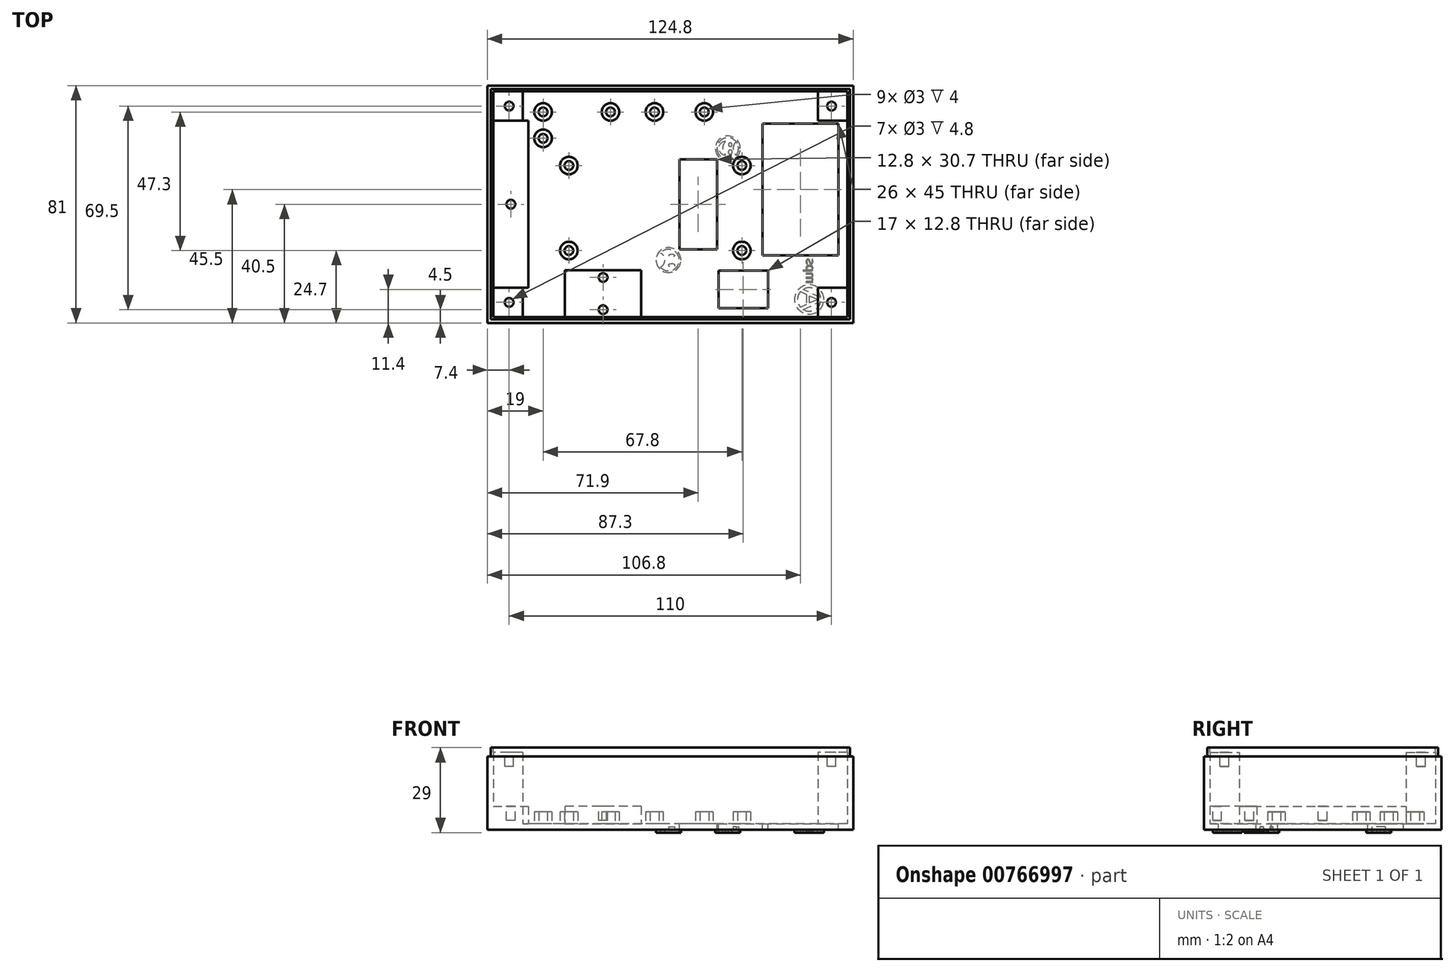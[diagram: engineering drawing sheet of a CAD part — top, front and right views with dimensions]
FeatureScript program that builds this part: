
annotation { "Feature Type Name" : "Feature", "Feature Type Description" : "" }
export const myFeature = defineFeature(function(context is Context, id is Id, definition is map)
    precondition{}
    {
        {
            var Q0;
            Q0=qCreatedBy(makeId("Top.planeOp"),FACE);
            var sketch = newSketch(context, id + "F0", { "sketchPlane" : qUnion([Q0])});
            skLineSegment(sketch, "E0.bottom", {"start": v(62.4, -40.5) * mm, "end": v(-62.4, -40.5) * mm});
            skLineSegment(sketch, "E0.top", {"start": v(62.4, 40.5) * mm, "end": v(-62.4, 40.5) * mm});
            skLineSegment(sketch, "E0.left", {"start": v(62.4, -40.5) * mm, "end": v(62.4, 40.5) * mm});
            skLineSegment(sketch, "E0.right", {"start": v(-62.4, -40.5) * mm, "end": v(-62.4, 40.5) * mm});
            skPoint(sketch, "E0.middle", {"position": v(0, 0) * mm});
            skSolve(sketch);
        }
        {
            var Q0;
            Q0=qSketchRegion(id+"F0",true);
            extrude(context, id + "F1", {"entities" : qUnion([Q0]), "depth" : 25 * mm, "offsetDistance" : 25 * mm});
        }
        {
            var Q0;
            Q0=makeQuery(id+"F1.opExtrude","CAP_FACE",FACE,{"disambiguationData":[OSD([sQuery(id+"F0.wireOp",EDGE,"E0.bottom"),sQuery(id+"F0.wireOp",EDGE,"E0.top"),sQuery(id+"F0.wireOp",EDGE,"E0.left"),sQuery(id+"F0.wireOp",EDGE,"E0.right")])],"isStart":false});
            var sketch = newSketch(context, id + "F2", { "sketchPlane" : qUnion([Q0])});
            skLineSegment(sketch, "E1.bottom", {"start": v(61.25, -39.35) * mm, "end": v(-61.25, -39.35) * mm});
            skLineSegment(sketch, "E1.top", {"start": v(61.25, 39.35) * mm, "end": v(-61.25, 39.35) * mm});
            skLineSegment(sketch, "E1.left", {"start": v(61.25, -39.35) * mm, "end": v(61.25, 39.35) * mm});
            skLineSegment(sketch, "E1.right", {"start": v(-61.25, -39.35) * mm, "end": v(-61.25, 39.35) * mm});
            skPoint(sketch, "E1.middle", {"position": v(0, 0) * mm});
            skSolve(sketch);
        }
        {
            var Q0;
            Q0=qSketchRegion(id+"F2",true);
            extrude(context, id + "F3", {"entities" : qUnion([Q0]), "operationType" : NewBodyOperationType.ADD, "depth" : 3 * mm, "offsetDistance" : 25 * mm});
        }
        {
            var Q0;
            Q0=makeQuery(id+"F3.opExtrude","CAP_FACE",FACE,{"disambiguationData":[OSD([sQuery(id+"F2.wireOp",EDGE,"E1.bottom"),sQuery(id+"F2.wireOp",EDGE,"E1.top"),sQuery(id+"F2.wireOp",EDGE,"E1.left"),sQuery(id+"F2.wireOp",EDGE,"E1.right")])],"isStart":false});
            var sketch = newSketch(context, id + "F4", { "sketchPlane" : qUnion([Q0])});
            skLineSegment(sketch, "E2.bottom", {"start": v(60.4, -38.5) * mm, "end": v(-60.4, -38.5) * mm});
            skLineSegment(sketch, "E2.top", {"start": v(60.4, 38.5) * mm, "end": v(-60.4, 38.5) * mm});
            skLineSegment(sketch, "E2.left", {"start": v(60.4, -38.5) * mm, "end": v(60.4, 38.5) * mm});
            skLineSegment(sketch, "E2.right", {"start": v(-60.4, -38.5) * mm, "end": v(-60.4, 38.5) * mm});
            skPoint(sketch, "E2.middle", {"position": v(0, 0) * mm});
            skSolve(sketch);
        }
        {
            var Q0;
            Q0=qSketchRegion(id+"F4",true);
            extrude(context, id + "F5", {"entities" : qUnion([Q0]), "operationType" : NewBodyOperationType.REMOVE, "oppositeDirection" : true, "depth" : 26 * mm, "offsetDistance" : 25 * mm});
        }
        {
            var Q0;
            Q0=makeQuery(id+"F5.boolean.opBoolean","COPY",FACE,{"derivedFrom":makeQuery(id+"F5.opExtrude","CAP_FACE",FACE,{"disambiguationData":[OSD([sQuery(id+"F4.wireOp",EDGE,"E2.bottom"),sQuery(id+"F4.wireOp",EDGE,"E2.top"),sQuery(id+"F4.wireOp",EDGE,"E2.left"),sQuery(id+"F4.wireOp",EDGE,"E2.right")])],"isStart":false})});
            var sketch = newSketch(context, id + "F6", { "sketchPlane" : qUnion([Q0])});
            skLineSegment(sketch, "E3.bottom", {"start": v(-60.4, 38.5) * mm, "end": v(-50.4, 38.5) * mm});
            skLineSegment(sketch, "E3.top", {"start": v(-60.4, 28.5) * mm, "end": v(-50.4, 28.5) * mm});
            skLineSegment(sketch, "E3.left", {"start": v(-60.4, 38.5) * mm, "end": v(-60.4, 28.5) * mm});
            skLineSegment(sketch, "E3.right", {"start": v(-50.4, 38.5) * mm, "end": v(-50.4, 28.5) * mm});
            skLineSegment(sketch, "E4.bottom", {"start": v(-60.4, -38.5) * mm, "end": v(-50.4, -38.5) * mm});
            skLineSegment(sketch, "E4.top", {"start": v(-60.4, -28.5) * mm, "end": v(-50.4, -28.5) * mm});
            skLineSegment(sketch, "E4.left", {"start": v(-60.4, -38.5) * mm, "end": v(-60.4, -28.5) * mm});
            skLineSegment(sketch, "E4.right", {"start": v(-50.4, -38.5) * mm, "end": v(-50.4, -28.5) * mm});
            skLineSegment(sketch, "E5.bottom", {"start": v(60.4, -38.5) * mm, "end": v(50.4, -38.5) * mm});
            skLineSegment(sketch, "E5.top", {"start": v(60.4, -28.5) * mm, "end": v(50.4, -28.5) * mm});
            skLineSegment(sketch, "E5.left", {"start": v(60.4, -38.5) * mm, "end": v(60.4, -28.5) * mm});
            skLineSegment(sketch, "E5.right", {"start": v(50.4, -38.5) * mm, "end": v(50.4, -28.5) * mm});
            skLineSegment(sketch, "E6.bottom", {"start": v(60.4, 38.5) * mm, "end": v(50.4, 38.5) * mm});
            skLineSegment(sketch, "E6.top", {"start": v(60.4, 28.5) * mm, "end": v(50.4, 28.5) * mm});
            skLineSegment(sketch, "E6.left", {"start": v(60.4, 38.5) * mm, "end": v(60.4, 28.5) * mm});
            skLineSegment(sketch, "E6.right", {"start": v(50.4, 38.5) * mm, "end": v(50.4, 28.5) * mm});
            skSolve(sketch);
        }
        {
            var Q0;
            Q0=qSketchRegion(id+"F6",true);
            extrude(context, id + "F7", {"entities" : qUnion([Q0]), "operationType" : NewBodyOperationType.ADD, "depth" : 24.4 * mm, "offsetDistance" : 25 * mm});
        }
        {
            var Q0;
            Q0=makeQuery(id+"F7.opExtrude","CAP_FACE",FACE,{"disambiguationData":[OSD([sQuery(id+"F6.wireOp",EDGE,"E3.bottom"),sQuery(id+"F6.wireOp",EDGE,"E3.top"),sQuery(id+"F6.wireOp",EDGE,"E3.left"),sQuery(id+"F6.wireOp",EDGE,"E3.right")])],"isStart":false});
            var sketch = newSketch(context, id + "F8", { "sketchPlane" : qUnion([Q0])});
            skCircle(sketch, "E7", {"center": v(-55, 33.5) * mm, "radius": 1.5 * mm});
            skPoint(sketch, "E7.centerSnap0", {"position": v(-50.4, 33.5) * mm});
            skCircle(sketch, "E8", {"center": v(-55, -33.5) * mm, "radius": 1.5 * mm});
            skCircle(sketch, "E9", {"center": v(55, -33.5) * mm, "radius": 1.5 * mm});
            skCircle(sketch, "E10", {"center": v(55, 33.5) * mm, "radius": 1.5 * mm});
            skSolve(sketch);
        }
        {
            var Q0;
            Q0=qSketchRegion(id+"F8",true);
            extrude(context, id + "F9", {"entities" : qUnion([Q0]), "operationType" : NewBodyOperationType.REMOVE, "oppositeDirection" : true, "depth" : 4.8 * mm, "offsetDistance" : 25 * mm});
        }
        {
            var Q0;
            Q0=makeQuery(id+"F5.boolean.opBoolean","COPY",FACE,{"derivedFrom":makeQuery(id+"F5.opExtrude","CAP_FACE",FACE,{"disambiguationData":[OSD([sQuery(id+"F4.wireOp",EDGE,"E2.bottom"),sQuery(id+"F4.wireOp",EDGE,"E2.top"),sQuery(id+"F4.wireOp",EDGE,"E2.left"),sQuery(id+"F4.wireOp",EDGE,"E2.right")])],"isStart":false})});
            var sketch = newSketch(context, id + "F10", { "sketchPlane" : qUnion([Q0])});
            skLineSegment(sketch, "E11.bottom", {"start": v(31.4, 27.5) * mm, "end": v(57.4, 27.5) * mm});
            skLineSegment(sketch, "E11.top", {"start": v(31.4, -17.5) * mm, "end": v(57.4, -17.5) * mm});
            skLineSegment(sketch, "E11.left", {"start": v(31.4, 27.5) * mm, "end": v(31.4, -17.5) * mm});
            skLineSegment(sketch, "E11.right", {"start": v(57.4, 27.5) * mm, "end": v(57.4, -17.5) * mm});
            skLineSegment(sketch, "E12.bottom", {"start": v(16.4, -22.7) * mm, "end": v(33.4, -22.7) * mm});
            skLineSegment(sketch, "E12.top", {"start": v(16.4, -35.5) * mm, "end": v(33.4, -35.5) * mm});
            skLineSegment(sketch, "E12.left", {"start": v(16.4, -22.7) * mm, "end": v(16.4, -35.5) * mm});
            skLineSegment(sketch, "E12.right", {"start": v(33.4, -22.7) * mm, "end": v(33.4, -35.5) * mm});
            skLineSegment(sketch, "E13.bottom", {"start": v(15.9, -15.35) * mm, "end": v(3.1, -15.35) * mm});
            skLineSegment(sketch, "E13.top", {"start": v(15.9, 15.35) * mm, "end": v(3.1, 15.35) * mm});
            skLineSegment(sketch, "E13.left", {"start": v(15.9, -15.35) * mm, "end": v(15.9, 15.35) * mm});
            skLineSegment(sketch, "E13.right", {"start": v(3.1, -15.35) * mm, "end": v(3.1, 15.35) * mm});
            skPoint(sketch, "E13.middle", {"position": v(9.5, 0) * mm});
            skSolve(sketch);
        }
        {
            var Q0;
            Q0=qSketchRegion(id+"F10",true);
            extrude(context, id + "F11", {"entities" : qUnion([Q0]), "operationType" : NewBodyOperationType.REMOVE, "endBound" : BoundingType.THROUGH_ALL, "oppositeDirection" : true, "depth" : 25 * mm, "offsetDistance" : 25 * mm});
        }
        {
            var Q0;
            Q0=makeQuery(id+"F5.boolean.opBoolean","COPY",FACE,{"derivedFrom":makeQuery(id+"F5.opExtrude","CAP_FACE",FACE,{"disambiguationData":[OSD([sQuery(id+"F4.wireOp",EDGE,"E2.bottom"),sQuery(id+"F4.wireOp",EDGE,"E2.top"),sQuery(id+"F4.wireOp",EDGE,"E2.left"),sQuery(id+"F4.wireOp",EDGE,"E2.right")])],"isStart":false})});
            var sketch = newSketch(context, id + "F12", { "sketchPlane" : qUnion([Q0])});
            skCircle(sketch, "E14", {"center": v(24.4, 13.2) * mm, "radius": 3 * mm});
            skCircle(sketch, "E15", {"center": v(-34.6, 13.2) * mm, "radius": 3 * mm});
            skCircle(sketch, "E16", {"center": v(-34.6, -15.8) * mm, "radius": 3 * mm});
            skCircle(sketch, "E17", {"center": v(24.4, -15.8) * mm, "radius": 3 * mm});
            skCircle(sketch, "E18", {"center": v(-43.4, 31.5) * mm, "radius": 3 * mm});
            skCircle(sketch, "E19", {"center": v(-43.4, 22.5) * mm, "radius": 3 * mm});
            skCircle(sketch, "E20", {"center": v(-20.4, 31.5) * mm, "radius": 3 * mm});
            skCircle(sketch, "E21", {"center": v(-5.4, 31.5) * mm, "radius": 3 * mm});
            skCircle(sketch, "E22", {"center": v(11.6, 31.5) * mm, "radius": 3 * mm});
            skSolve(sketch);
        }
        {
            var Q0;
            Q0=qSketchRegion(id+"F12",true);
            extrude(context, id + "F13", {"entities" : qUnion([Q0]), "operationType" : NewBodyOperationType.ADD, "depth" : 4 * mm, "offsetDistance" : 25 * mm});
        }
        {
            var Q0;
            Q0=makeQuery(id+"F5.boolean.opBoolean","COPY",FACE,{"derivedFrom":makeQuery(id+"F5.opExtrude","CAP_FACE",FACE,{"disambiguationData":[OSD([sQuery(id+"F4.wireOp",EDGE,"E2.bottom"),sQuery(id+"F4.wireOp",EDGE,"E2.top"),sQuery(id+"F4.wireOp",EDGE,"E2.left"),sQuery(id+"F4.wireOp",EDGE,"E2.right")])],"isStart":false})});
            var sketch = newSketch(context, id + "F14", { "sketchPlane" : qUnion([Q0])});
            skCircle(sketch, "E23", {"center": v(-34.6, -15.8) * mm, "radius": 1.5 * mm});
            skCircle(sketch, "E24", {"center": v(24.4, -15.8) * mm, "radius": 1.5 * mm});
            skCircle(sketch, "E25", {"center": v(-34.6, 13.2) * mm, "radius": 1.5 * mm});
            skCircle(sketch, "E26", {"center": v(24.4, 13.2) * mm, "radius": 1.5 * mm});
            skCircle(sketch, "E27", {"center": v(11.6, 31.5) * mm, "radius": 1.5 * mm});
            skCircle(sketch, "E28", {"center": v(-5.4, 31.5) * mm, "radius": 1.5 * mm});
            skCircle(sketch, "E29", {"center": v(-20.4, 31.5) * mm, "radius": 1.5 * mm});
            skCircle(sketch, "E30", {"center": v(-43.4, 22.5) * mm, "radius": 1.5 * mm});
            skCircle(sketch, "E31", {"center": v(-43.4, 31.5) * mm, "radius": 1.5 * mm});
            skSolve(sketch);
        }
        {
            var Q0;
            Q0=qSketchRegion(id+"F14",true);
            extrude(context, id + "F15", {"entities" : qUnion([Q0]), "operationType" : NewBodyOperationType.REMOVE, "depth" : 4.8 * mm, "offsetDistance" : 25 * mm});
        }
        {
            var Q0;
            Q0=makeQuery(id+"F5.boolean.opBoolean","COPY",FACE,{"derivedFrom":makeQuery(id+"F5.opExtrude","CAP_FACE",FACE,{"disambiguationData":[OSD([sQuery(id+"F4.wireOp",EDGE,"E2.bottom"),sQuery(id+"F4.wireOp",EDGE,"E2.top"),sQuery(id+"F4.wireOp",EDGE,"E2.left"),sQuery(id+"F4.wireOp",EDGE,"E2.right")])],"isStart":false})});
            var sketch = newSketch(context, id + "F16", { "sketchPlane" : qUnion([Q0])});
            skLineSegment(sketch, "E32.bottom", {"start": v(-60.4, -28.5) * mm, "end": v(-48.4, -28.5) * mm});
            skLineSegment(sketch, "E32.top", {"start": v(-60.4, 28.5) * mm, "end": v(-48.4, 28.5) * mm});
            skLineSegment(sketch, "E32.left", {"start": v(-60.4, -28.5) * mm, "end": v(-60.4, 28.5) * mm});
            skLineSegment(sketch, "E32.right", {"start": v(-48.4, -28.5) * mm, "end": v(-48.4, 28.5) * mm});
            skSolve(sketch);
        }
        {
            var Q0;
            Q0=qSketchRegion(id+"F16",true);
            extrude(context, id + "F17", {"entities" : qUnion([Q0]), "operationType" : NewBodyOperationType.ADD, "depth" : 6 * mm, "offsetDistance" : 25 * mm});
        }
        {
            var Q0;
            Q0=makeQuery(id+"F17.opExtrude","CAP_FACE",FACE,{"disambiguationData":[OSD([sQuery(id+"F16.wireOp",EDGE,"E32.bottom"),sQuery(id+"F16.wireOp",EDGE,"E32.top"),sQuery(id+"F16.wireOp",EDGE,"E32.left"),sQuery(id+"F16.wireOp",EDGE,"E32.right")])],"isStart":false});
            var sketch = newSketch(context, id + "F18", { "sketchPlane" : qUnion([Q0])});
            skCircle(sketch, "E33", {"center": v(-54.4, 0) * mm, "radius": 1.5 * mm});
            skPoint(sketch, "E33.centerSnap0", {"position": v(-48.4, 0) * mm});
            skSolve(sketch);
        }
        {
            var Q0;
            Q0=qSketchRegion(id+"F18",true);
            extrude(context, id + "F19", {"entities" : qUnion([Q0]), "operationType" : NewBodyOperationType.REMOVE, "oppositeDirection" : true, "depth" : 4.8 * mm, "offsetDistance" : 25 * mm});
        }
        {
            var Q0;
            Q0=makeQuery(id+"F5.boolean.opBoolean","COPY",FACE,{"derivedFrom":makeQuery(id+"F5.opExtrude","CAP_FACE",FACE,{"disambiguationData":[OSD([sQuery(id+"F4.wireOp",EDGE,"E2.bottom"),sQuery(id+"F4.wireOp",EDGE,"E2.top"),sQuery(id+"F4.wireOp",EDGE,"E2.left"),sQuery(id+"F4.wireOp",EDGE,"E2.right")])],"isStart":false})});
            var sketch = newSketch(context, id + "F20", { "sketchPlane" : qUnion([Q0])});
            skLineSegment(sketch, "E34.bottom", {"start": v(-35.93, -22.5) * mm, "end": v(-9.93, -22.5) * mm});
            skLineSegment(sketch, "E34.top", {"start": v(-35.93, -38.5) * mm, "end": v(-9.93, -38.5) * mm});
            skLineSegment(sketch, "E34.left", {"start": v(-35.93, -22.5) * mm, "end": v(-35.93, -38.5) * mm});
            skLineSegment(sketch, "E34.right", {"start": v(-9.93, -22.5) * mm, "end": v(-9.93, -38.5) * mm});
            skSolve(sketch);
        }
        {
            var Q0;
            Q0=qSketchRegion(id+"F20",true);
            extrude(context, id + "F21", {"entities" : qUnion([Q0]), "operationType" : NewBodyOperationType.ADD, "depth" : 6 * mm, "offsetDistance" : 25 * mm});
        }
        {
            var Q0;
            Q0=makeQuery(id+"F21.opExtrude","CAP_FACE",FACE,{"disambiguationData":[OSD([sQuery(id+"F20.wireOp",EDGE,"E34.bottom"),sQuery(id+"F20.wireOp",EDGE,"E34.top"),sQuery(id+"F20.wireOp",EDGE,"E34.left"),sQuery(id+"F20.wireOp",EDGE,"E34.right")])],"isStart":false});
            var sketch = newSketch(context, id + "F22", { "sketchPlane" : qUnion([Q0])});
            skCircle(sketch, "E35", {"center": v(-22.93, -25) * mm, "radius": 1.5 * mm});
            skPoint(sketch, "E35.centerSnap0", {"position": v(-22.93, -22.5) * mm});
            skPoint(sketch, "E35.perimeterSnap0", {"position": v(-22.93, -22.5) * mm});
            skPoint(sketch, "E35.perimeterSnap1", {"position": v(-35.93, -30.5) * mm});
            skCircle(sketch, "E36", {"center": v(-22.93, -36) * mm, "radius": 1.5 * mm});
            skSolve(sketch);
        }
        {
            var Q0;
            Q0=qSketchRegion(id+"F22",true);
            extrude(context, id + "F23", {"entities" : qUnion([Q0]), "operationType" : NewBodyOperationType.REMOVE, "oppositeDirection" : true, "depth" : 4.8 * mm, "offsetDistance" : 25 * mm});
        }
        {
            var Q0;
            Q0=makeQuery(id+"F1.opExtrude","CAP_FACE",FACE,{"disambiguationData":[OSD([sQuery(id+"F0.wireOp",EDGE,"E0.bottom"),sQuery(id+"F0.wireOp",EDGE,"E0.top"),sQuery(id+"F0.wireOp",EDGE,"E0.left"),sQuery(id+"F0.wireOp",EDGE,"E0.right")])],"isStart":true});
            var sketch = newSketch(context, id + "F24", { "sketchPlane" : qUnion([Q0])});
            skCircle(sketch, "E37", {"center": v(47.4, 32.5) * mm, "radius": 5 * mm});
            skCircle(sketch, "E38", {"center": v(47.4, 32.5) * mm, "radius": 4 * mm});
            skSolve(sketch);
        }
        {
            var Q0;
            Q0 = qSketchRegion(id + "F24", true);
            extrude(context, id + "F25", {"entities" : qUnion([Q0]), "operationType" : NewBodyOperationType.ADD, "depth" : 1 * mm, "offsetDistance" : 25 * mm});
        }
        {
            var Q0;
            {var subQ0=sQuery(id+"F0.wireOp",EDGE,"E0.bottom");var subQ1=sQuery(id+"F0.wireOp",EDGE,"E0.right");var subQ2=sQuery(id+"F0.wireOp",EDGE,"E0.top");var subQ3=sQuery(id+"F0.wireOp",EDGE,"E0.left");Q0=makeQuery(id+"F25.boolean.opBoolean","SPLIT",FACE,{"disambiguationData":[TD([makeQuery(id+"F1.opExtrude","SWEPT_FACE",FACE,{"disambiguationData":[OSD([subQ0])]})])],"derivedFrom":makeQuery(id+"F1.opExtrude","CAP_FACE",FACE,{"disambiguationData":[OSD([subQ0,subQ2,subQ3,subQ1])],"isStart":true})});}
            var sketch = newSketch(context, id + "F26", { "sketchPlane" : qUnion([Q0])});
            skText(sketch, "E39", { "text": "mps", "fontName": "OpenSans-Regular.ttf"});
            const initialGuessF26  = {"E39": [0.04636, 0.0271, 0, -1, 0.00304]};
            skSetInitialGuess(sketch, initialGuessF26);
            skSolve(sketch);
        }
        {
            var Q0;
            Q0 = qSketchRegion(id + "F26", true);
            extrude(context, id + "F27", {"entities" : qUnion([Q0]), "operationType" : NewBodyOperationType.ADD, "depth" : 1 * mm, "offsetDistance" : 25 * mm});
        }
        {
            var Q0;
            {var subQ12=sQuery(id+"F0.wireOp",EDGE,"E0.right");var subQ14=sQuery(id+"F0.wireOp",EDGE,"E0.top");var subQ16=sQuery(id+"F0.wireOp",EDGE,"E0.left");var subQ18=sQuery(id+"F0.wireOp",EDGE,"E0.bottom");var subQ19=makeQuery(id+"F1.opExtrude","SWEPT_FACE",FACE,{"disambiguationData":[OSD([subQ18])]});Q0=makeQuery(id+"F27.boolean.opBoolean","SPLIT",FACE,{"disambiguationData":[TD([subQ19])],"derivedFrom":makeQuery(id+"F25.boolean.opBoolean","SPLIT",FACE,{"disambiguationData":[TD([subQ19])],"derivedFrom":makeQuery(id+"F1.opExtrude","CAP_FACE",FACE,{"disambiguationData":[OSD([subQ18,subQ14,subQ16,subQ12])],"isStart":true})})});}
            var sketch = newSketch(context, id + "F28", { "sketchPlane" : qUnion([Q0])});
            skLineSegment(sketch, "E40", {"start": v(44.91, 36.12) * mm, "end": v(51.52, 33.06) * mm});
            skLineSegment(sketch, "E41", {"start": v(51.52, 33.06) * mm, "end": v(51.52, 31.97) * mm});
            skLineSegment(sketch, "E42", {"start": v(51.52, 31.97) * mm, "end": v(45.1, 28.97) * mm});
            skLineSegment(sketch, "E43", {"start": v(45.1, 28.97) * mm, "end": v(44.19, 29.7) * mm});
            skLineSegment(sketch, "E44", {"start": v(44.19, 29.7) * mm, "end": v(46.4, 30.75) * mm});
            skLineSegment(sketch, "E45", {"start": v(46.4, 30.75) * mm, "end": v(46.4, 34.26) * mm});
            skLineSegment(sketch, "E46", {"start": v(46.4, 34.26) * mm, "end": v(44.17, 35.3) * mm});
            skLineSegment(sketch, "E47", {"start": v(44.17, 35.3) * mm, "end": v(44.91, 36.12) * mm});
            skLineSegment(sketch, "E48", {"start": v(50.23, 32.5) * mm, "end": v(47.48, 33.76) * mm});
            skLineSegment(sketch, "E49", {"start": v(47.48, 33.76) * mm, "end": v(47.48, 31.24) * mm});
            skLineSegment(sketch, "E50", {"start": v(47.48, 31.24) * mm, "end": v(50.23, 32.5) * mm});
            skSolve(sketch);
        }
        {
            var Q0;
            Q0=makeQuery(id+"F28.imprint","IMPRINT",FACE,{"disambiguationData":[TD([[makeQuery(id+"F28.imprint","IMPRINT",EDGE,{"derivedFrom":sQuery(id+"F28.wireOp",EDGE,"E40")}),-1.0]])]});
            extrude(context, id + "F29", {"entities" : qUnion([Q0]), "operationType" : NewBodyOperationType.ADD, "depth" : 1 * mm, "offsetDistance" : 25 * mm});
        }
        {
            var Q0;
            {var subQ12=sQuery(id+"F0.wireOp",EDGE,"E0.right");var subQ14=sQuery(id+"F0.wireOp",EDGE,"E0.top");var subQ16=sQuery(id+"F0.wireOp",EDGE,"E0.left");var subQ18=sQuery(id+"F0.wireOp",EDGE,"E0.bottom");var subQ19=makeQuery(id+"F1.opExtrude","SWEPT_FACE",FACE,{"disambiguationData":[OSD([subQ18])]});Q0=makeQuery(id+"F27.boolean.opBoolean","SPLIT",FACE,{"disambiguationData":[TD([subQ19])],"derivedFrom":makeQuery(id+"F25.boolean.opBoolean","SPLIT",FACE,{"disambiguationData":[TD([subQ19])],"derivedFrom":makeQuery(id+"F1.opExtrude","CAP_FACE",FACE,{"disambiguationData":[OSD([subQ18,subQ14,subQ16,subQ12])],"isStart":true})})});}
            var sketch = newSketch(context, id + "F30", { "sketchPlane" : qUnion([Q0])});
            skCircle(sketch, "E51", {"center": v(19.61, -19.06) * mm, "radius": 4.25 * mm});
            skCircle(sketch, "E52", {"center": v(-0.61, 19.06) * mm, "radius": 4.25 * mm});
            skLineSegment(sketch, "E53", {"start": v(15.9, -15.35) * mm, "end": v(19.61, -19.06) * mm, "construction": true});
            skLineSegment(sketch, "E54", {"start": v(3.1, 15.35) * mm, "end": v(-0.61, 19.06) * mm, "construction": true});
            skCircle(sketch, "E55", {"center": v(-0.61, 19.06) * mm, "radius": 3.65 * mm});
            skCircle(sketch, "E56", {"center": v(19.61, -19.06) * mm, "radius": 3.65 * mm});
            skSolve(sketch);
        }
        {
            var Q0;
            Q0 = qSketchRegion(id + "F30", true);
            extrude(context, id + "F31", {"entities" : qUnion([Q0]), "operationType" : NewBodyOperationType.ADD, "depth" : 1 * mm, "offsetDistance" : 25 * mm});
        }
        {
            var Q0;
            {var subQ34=sQuery(id+"F0.wireOp",EDGE,"E0.right");var subQ38=sQuery(id+"F0.wireOp",EDGE,"E0.top");var subQ42=sQuery(id+"F0.wireOp",EDGE,"E0.left");var subQ47=sQuery(id+"F0.wireOp",EDGE,"E0.bottom");var subQ48=makeQuery(id+"F1.opExtrude","SWEPT_FACE",FACE,{"disambiguationData":[OSD([subQ47])]});Q0=makeQuery(id+"F31.boolean.opBoolean","SPLIT",FACE,{"disambiguationData":[TD([subQ48])],"derivedFrom":makeQuery(id+"F27.boolean.opBoolean","SPLIT",FACE,{"disambiguationData":[TD([subQ48])],"derivedFrom":makeQuery(id+"F25.boolean.opBoolean","SPLIT",FACE,{"disambiguationData":[TD([subQ48])],"derivedFrom":makeQuery(id+"F1.opExtrude","CAP_FACE",FACE,{"disambiguationData":[OSD([subQ47,subQ38,subQ42,subQ34])],"isStart":true})})})});}
            var sketch = newSketch(context, id + "F32", { "sketchPlane" : qUnion([Q0])});
            skArc(sketch, "E57", {"start": v(22.46, -16.78) * mm, "mid": v(21.42, -19.05) * mm, "end": v(22.46, -21.32) * mm});
            skArc(sketch, "E58", {"start": v(22.46, -21.32) * mm, "mid": v(23.3, -19.05) * mm, "end": v(22.46, -16.78) * mm});
            skSolve(sketch);
        }
        {
            var Q0;
            Q0 = qSketchRegion(id + "F32", true);
            extrude(context, id + "F33", {"entities" : qUnion([Q0]), "operationType" : NewBodyOperationType.REMOVE, "oppositeDirection" : true, "depth" : 1 * mm, "offsetDistance" : 25 * mm});
        }
        {
            var Q0;
            {var subQ34=sQuery(id+"F0.wireOp",EDGE,"E0.right");var subQ38=sQuery(id+"F0.wireOp",EDGE,"E0.top");var subQ42=sQuery(id+"F0.wireOp",EDGE,"E0.left");var subQ47=sQuery(id+"F0.wireOp",EDGE,"E0.bottom");var subQ48=makeQuery(id+"F1.opExtrude","SWEPT_FACE",FACE,{"disambiguationData":[OSD([subQ47])]});Q0=makeQuery(id+"F31.boolean.opBoolean","SPLIT",FACE,{"disambiguationData":[TD([subQ48])],"derivedFrom":makeQuery(id+"F27.boolean.opBoolean","SPLIT",FACE,{"disambiguationData":[TD([subQ48])],"derivedFrom":makeQuery(id+"F25.boolean.opBoolean","SPLIT",FACE,{"disambiguationData":[TD([subQ48])],"derivedFrom":makeQuery(id+"F1.opExtrude","CAP_FACE",FACE,{"disambiguationData":[OSD([subQ47,subQ38,subQ42,subQ34])],"isStart":true})})})});}
            var sketch = newSketch(context, id + "F34", { "sketchPlane" : qUnion([Q0])});
            skArc(sketch, "E59", {"start": v(-3.67, 16.54) * mm, "mid": v(-1.88, 19.07) * mm, "end": v(-3.67, 21.6) * mm});
            skArc(sketch, "E60", {"start": v(-3.67, 21.6) * mm, "mid": v(-4.55, 19.07) * mm, "end": v(-3.67, 16.54) * mm});
            skSolve(sketch);
        }
        {
            var Q0;
            Q0 = qSketchRegion(id + "F34", true);
            extrude(context, id + "F35", {"entities" : qUnion([Q0]), "operationType" : NewBodyOperationType.ADD, "depth" : 1 * mm, "offsetDistance" : 25 * mm});
        }
        {
            var Q0;
            {var subQ34=sQuery(id+"F0.wireOp",EDGE,"E0.right");var subQ38=sQuery(id+"F0.wireOp",EDGE,"E0.top");var subQ42=sQuery(id+"F0.wireOp",EDGE,"E0.left");var subQ47=sQuery(id+"F0.wireOp",EDGE,"E0.bottom");var subQ48=makeQuery(id+"F1.opExtrude","SWEPT_FACE",FACE,{"disambiguationData":[OSD([subQ47])]});Q0=makeQuery(id+"F31.boolean.opBoolean","SPLIT",FACE,{"disambiguationData":[TD([subQ48])],"derivedFrom":makeQuery(id+"F27.boolean.opBoolean","SPLIT",FACE,{"disambiguationData":[TD([subQ48])],"derivedFrom":makeQuery(id+"F25.boolean.opBoolean","SPLIT",FACE,{"disambiguationData":[TD([subQ48])],"derivedFrom":makeQuery(id+"F1.opExtrude","CAP_FACE",FACE,{"disambiguationData":[OSD([subQ47,subQ38,subQ42,subQ34])],"isStart":true})})})});}
            var sketch = newSketch(context, id + "F36", { "sketchPlane" : qUnion([Q0])});
            skEllipse(sketch, "E61", {"center": v(0.47, 20.82) * mm, "majorRadius": 1.05 * mm, "minorRadius": 0.58 * mm, "majorAxis": v(-1, 0)});
            skEllipse(sketch, "E62", {"center": v(0.47, 17.5) * mm, "majorRadius": 1 * mm, "minorRadius": 0.5 * mm, "majorAxis": v(-1, 0)});
            skSolve(sketch);
        }
        {
            var Q0;
            Q0 = qSketchRegion(id + "F36", true);
            extrude(context, id + "F37", {"entities" : qUnion([Q0]), "operationType" : NewBodyOperationType.REMOVE, "oppositeDirection" : true, "depth" : 1 * mm, "offsetDistance" : 25 * mm});
        }
        {
            var Q0;
            {var subQ34=sQuery(id+"F0.wireOp",EDGE,"E0.right");var subQ38=sQuery(id+"F0.wireOp",EDGE,"E0.top");var subQ42=sQuery(id+"F0.wireOp",EDGE,"E0.left");var subQ47=sQuery(id+"F0.wireOp",EDGE,"E0.bottom");var subQ48=makeQuery(id+"F1.opExtrude","SWEPT_FACE",FACE,{"disambiguationData":[OSD([subQ47])]});Q0=makeQuery(id+"F31.boolean.opBoolean","SPLIT",FACE,{"disambiguationData":[TD([subQ48])],"derivedFrom":makeQuery(id+"F27.boolean.opBoolean","SPLIT",FACE,{"disambiguationData":[TD([subQ48])],"derivedFrom":makeQuery(id+"F25.boolean.opBoolean","SPLIT",FACE,{"disambiguationData":[TD([subQ48])],"derivedFrom":makeQuery(id+"F1.opExtrude","CAP_FACE",FACE,{"disambiguationData":[OSD([subQ47,subQ38,subQ42,subQ34])],"isStart":true})})})});}
            var sketch = newSketch(context, id + "F38", { "sketchPlane" : qUnion([Q0])});
            skCircle(sketch, "E63", {"center": v(20.46, -17.82) * mm, "radius": 0.7 * mm});
            skCircle(sketch, "E64", {"center": v(20.46, -20.33) * mm, "radius": 0.62 * mm});
            skArc(sketch, "E65", {"start": v(18.9, -16.8) * mm, "mid": v(16.55, -19.13) * mm, "end": v(18.9, -21.48) * mm});
            skArc(sketch, "E66", {"start": v(18.9, -16.8) * mm, "mid": v(17.9, -19.13) * mm, "end": v(18.9, -21.48) * mm});
            skSolve(sketch);
        }
        {
            var Q0;
            Q0 = qSketchRegion(id + "F38", true);
            extrude(context, id + "F39", {"entities" : qUnion([Q0]), "operationType" : NewBodyOperationType.ADD, "depth" : 1 * mm, "offsetDistance" : 25 * mm});
        }
    });
